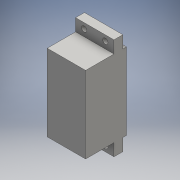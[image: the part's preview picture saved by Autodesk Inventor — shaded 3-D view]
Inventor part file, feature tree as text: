
AUTODESK INVENTOR PART (.ipt)
format: ipt  version: 2016 (Build 200138000, 138)  size: 135,680 bytes
history: native  units: mm
features: extrude x5, sketch x5, other x1
ambient origin geometry x8: Origin, YZ Plane, XZ Plane, XY Plane, X Axis, Y Axis, Z Axis, Center Point
bodies: Body1 (feature_tree)
feature tree (11):
  other  "ソリッド1"
  extrude  "押し出し1"  Depth=21.65mm
  extrude  "押し出し2"  Depth=43.3mm
  extrude  "押し出し3"  Depth=16.0mm TaperAngle=0.0deg
  extrude  "押し出し4"  Depth=57.15mm
  extrude  "押し出し5"  Depth=5.0mm TaperAngle=0.0deg
  sketch  "スケッチ1"
  sketch  "スケッチ2"
  sketch  "スケッチ3"
  sketch  "スケッチ4"
  sketch  "スケッチ5"
